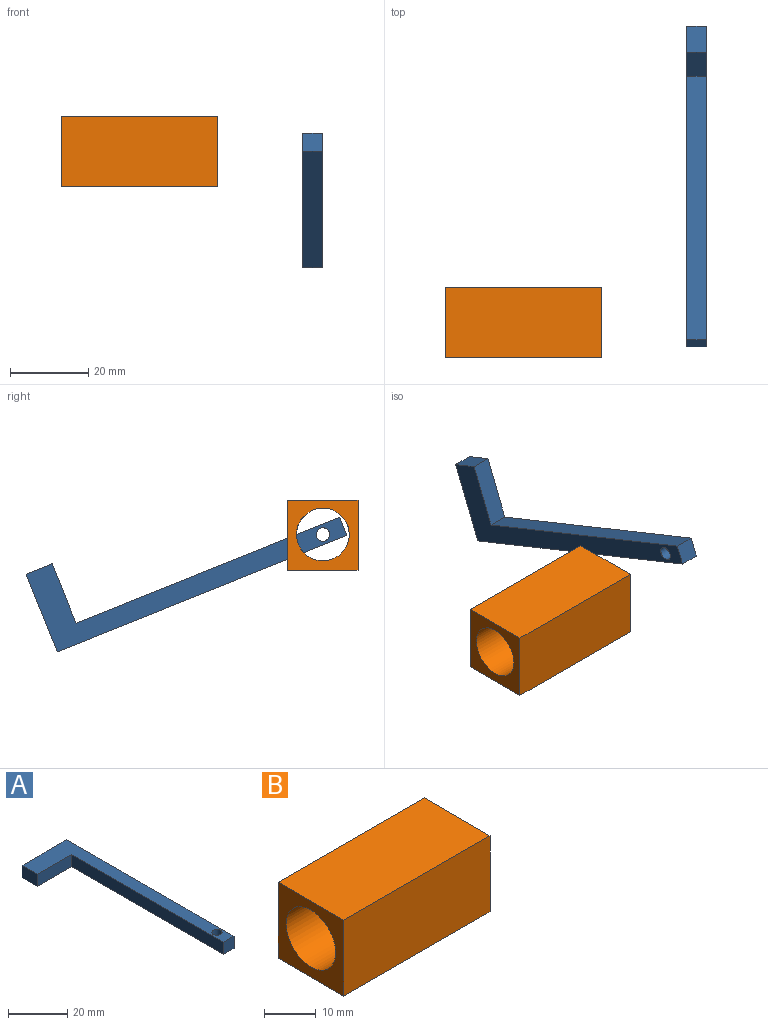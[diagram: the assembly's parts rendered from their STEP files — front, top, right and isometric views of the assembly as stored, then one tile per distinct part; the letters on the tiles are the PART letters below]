
ASSEMBLY  parts=2 mates=1
PART A: 9 faces, bbox 21.5x80x5 mm
  f0: plane 5.05x5mm, normal (0,-1,0), area 25.2mm2, adj f1,f6,f7,f8
  f1: plane 80x5mm, normal (1,0,0), area 400mm2, adj f0,f2,f7,f8
  f2: plane 21.49x5mm, normal (0,1,0), area 107.5mm2, adj f1,f3,f7,f8
  f3: plane 7.21x5mm, normal (-1,0,0), area 36.1mm2, adj f2,f4,f7,f8
  f4: plane 16.44x5mm, normal (0,-1,0), area 82.2mm2, adj f3,f6,f7,f8
  f5: cylinder r=1.72mm len=5mm, axis (0,0,-1), area 54mm2, adj f7,f8
  f6: plane 72.79x5mm, normal (-1,0,0), area 363.9mm2, adj f0,f4,f7,f8
  f7: plane 80x21.49mm, normal (0,0,1), area 513.2mm2, adj f0,f1,f2,f3,f4,f5,f6
  f8: plane 80x21.49mm, normal (0,0,-1), area 513.2mm2, adj f0,f1,f2,f3,f4,f5,f6
PART B: 7 faces, bbox 40x18x18 mm
  f0: plane 40x18mm, normal (0,1,0), area 720mm2, adj f1,f3,f4,f5
  f1: plane 18x18mm, normal (-1,0,0), area 180.4mm2, adj f0,f2,f4,f5,f6
  f2: plane 40x18mm, normal (0,-1,0), area 720mm2, adj f1,f3,f4,f5
  f3: plane 18x18mm, normal (1,0,0), area 180.4mm2, adj f0,f2,f4,f5,f6
  f4: plane 40x18mm, normal (0,0,1), area 720mm2, adj f0,f1,f2,f3
  f5: plane 40x18mm, normal (0,0,-1), area 720mm2, adj f0,f1,f2,f3
  f6: cylinder r=6.76mm len=40mm, axis (-1,0,0), area 1699.1mm2, adj f1,f3
PLACE A rot(axis=(-0.19,0.96,-0.19),92.1deg) t=(61.76,-6.17,-9.07)mm
PLACE B t=(20,0,-18)mm
MATE cylindrical A.f5 <-> B.f6  axis (-1,0,0) through (64.26,0,-8.83)mm
